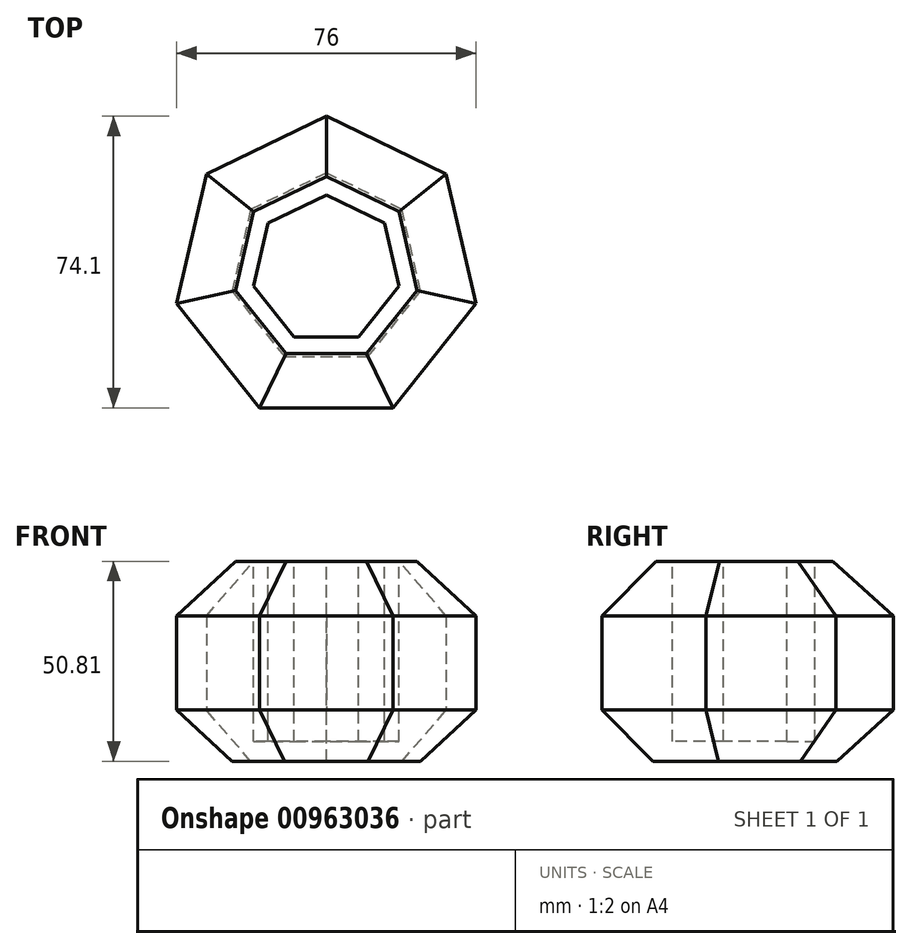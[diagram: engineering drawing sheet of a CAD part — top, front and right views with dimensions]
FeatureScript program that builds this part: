
annotation { "Feature Type Name" : "Feature", "Feature Type Description" : "" }
export const myFeature = defineFeature(function(context is Context, id is Id, definition is map)
    precondition{}
    {
        {
            var Q0;
            Q0=qCreatedBy(makeId("Top.planeOp"),FACE);
            var sketch = newSketch(context, id + "F0", { "sketchPlane" : qUnion([Q0])});
            skCircle(sketch, "E0.cCircle", {"center": v(0, 0) * mm, "radius": 35.12 * mm, "construction": true});
            skLineSegment(sketch, "E0.0", {"start": v(16.91, -35.12) * mm, "end": v(-16.91, -35.12) * mm});
            skLineSegment(sketch, "E0.1", {"start": v(-16.91, -35.12) * mm, "end": v(-38, -8.67) * mm});
            skLineSegment(sketch, "E0.2", {"start": v(-38, -8.67) * mm, "end": v(-30.47, 24.3) * mm});
            skLineSegment(sketch, "E0.3", {"start": v(-30.47, 24.3) * mm, "end": v(0, 38.98) * mm});
            skLineSegment(sketch, "E0.4", {"start": v(0, 38.98) * mm, "end": v(30.47, 24.3) * mm});
            skLineSegment(sketch, "E0.5", {"start": v(30.47, 24.3) * mm, "end": v(38, -8.67) * mm});
            skLineSegment(sketch, "E0.6", {"start": v(38, -8.67) * mm, "end": v(16.91, -35.12) * mm});
            skPoint(sketch, "E0.0.midPoint", {"position": v(0, -35.12) * mm});
            skSolve(sketch);
        }
        {
            var Q0;
            Q0 = qSketchRegion(id + "F0", true);
            extrude(context, id + "F1", {"entities" : qUnion([Q0]), "depth" : 60 * mm, "offsetDistance" : 25 * mm});
        }
        {
            var Q0;
            Q0=makeQuery(id+"F1.opExtrude","CAP_FACE",FACE,{"disambiguationData":[OSD([sQuery(id+"F0.wireOp",EDGE,"E0.0"),sQuery(id+"F0.wireOp",EDGE,"E0.1"),sQuery(id+"F0.wireOp",EDGE,"E0.2"),sQuery(id+"F0.wireOp",EDGE,"E0.3"),sQuery(id+"F0.wireOp",EDGE,"E0.4"),sQuery(id+"F0.wireOp",EDGE,"E0.5"),sQuery(id+"F0.wireOp",EDGE,"E0.6")])],"isStart":true});
            var Q1;
            Q1=makeQuery(id+"F1.opExtrude","CAP_FACE",FACE,{"disambiguationData":[OSD([sQuery(id+"F0.wireOp",EDGE,"E0.0"),sQuery(id+"F0.wireOp",EDGE,"E0.1"),sQuery(id+"F0.wireOp",EDGE,"E0.2"),sQuery(id+"F0.wireOp",EDGE,"E0.3"),sQuery(id+"F0.wireOp",EDGE,"E0.4"),sQuery(id+"F0.wireOp",EDGE,"E0.5"),sQuery(id+"F0.wireOp",EDGE,"E0.6")])],"isStart":false});
            chamfer(context, id + "F2", {"entities" : qUnion([Q0, Q1]), "width" : 18 * mm, "tangentPropagation" : true});
        }
        {
            var Q0;
            Q0=makeQuery(id+"F1.opExtrude","CAP_FACE",FACE,{"disambiguationData":[OSD([sQuery(id+"F0.wireOp",EDGE,"E0.0"),sQuery(id+"F0.wireOp",EDGE,"E0.1"),sQuery(id+"F0.wireOp",EDGE,"E0.2"),sQuery(id+"F0.wireOp",EDGE,"E0.3"),sQuery(id+"F0.wireOp",EDGE,"E0.4"),sQuery(id+"F0.wireOp",EDGE,"E0.5"),sQuery(id+"F0.wireOp",EDGE,"E0.6")])],"isStart":false});
            var sketch = newSketch(context, id + "F3", { "sketchPlane" : qUnion([Q0])});
            skSolve(sketch);
        }
        {
            var Q0;
            {var subQ0=sQuery(id+"F0.wireOp",EDGE,"E0.6");var subQ1=sQuery(id+"F0.wireOp",EDGE,"E0.5");var subQ2=sQuery(id+"F0.wireOp",EDGE,"E0.4");var subQ3=sQuery(id+"F0.wireOp",EDGE,"E0.3");var subQ4=sQuery(id+"F0.wireOp",EDGE,"E0.2");var subQ5=sQuery(id+"F0.wireOp",EDGE,"E0.1");var subQ6=sQuery(id+"F0.wireOp",EDGE,"E0.0");var subQ7=makeQuery(id+"F1.opExtrude","CAP_FACE",FACE,{"disambiguationData":[OSD([subQ6,subQ5,subQ4,subQ3,subQ2,subQ1,subQ0])],"isStart":false});Q0=makeQuery(id+"F3.imprint","IMPRINT",FACE,{"disambiguationData":[TD([[makeQuery(id+"F3.imprint","IMPRINT",EDGE,{"derivedFrom":makeQuery(id+"F2.opChamfer","BLEND_EDGE",EDGE,{"blendedFrom":[makeQuery(id+"F1.opExtrude","CAP_EDGE",EDGE,{"disambiguationData":[OSD([subQ6])],"isStart":false}),subQ7],"blendedInto":[subQ7]})}),1.0]])]});}
            extrude(context, id + "F4", {"entities" : qUnion([Q0]), "operationType" : NewBodyOperationType.REMOVE, "oppositeDirection" : true, "depth" : 50 * mm, "offsetDistance" : 25 * mm});
        }
        {
            var Q0;
            Q0=qCreatedBy(makeId("Front.planeOp"),FACE);
            cPlane(context, id + "F5", {"entities" : qUnion([Q0]), "cplaneType" : CPlaneType.OFFSET, "offset" : 45 * mm, "width" : 150 * mm, "height" : 150 * mm});
        }
        {
            var Q0;
            Q0=qCreatedBy(id+"F5.planeOp",FACE);
            var sketch = newSketch(context, id + "F6", { "sketchPlane" : qUnion([Q0])});
            skLineSegment(sketch, "E1.bottom", {"start": v(-28.5, 55.81) * mm, "end": v(30.37, 55.81) * mm});
            skLineSegment(sketch, "E1.top", {"start": v(-28.5, 65.1) * mm, "end": v(30.37, 65.1) * mm});
            skLineSegment(sketch, "E1.left", {"start": v(-28.5, 55.81) * mm, "end": v(-28.5, 65.1) * mm});
            skLineSegment(sketch, "E1.right", {"start": v(30.37, 55.81) * mm, "end": v(30.37, 65.1) * mm});
            skSolve(sketch);
        }
        {
            var Q0;
            Q0 = qSketchRegion(id + "F6", true);
            extrude(context, id + "F7", {"entities" : qUnion([Q0]), "operationType" : NewBodyOperationType.REMOVE, "oppositeDirection" : true, "depth" : 90 * mm, "offsetDistance" : 25 * mm});
        }
        {
            var Q0;
            Q0=qCreatedBy(id+"F5.planeOp",FACE);
            var sketch = newSketch(context, id + "F8", { "sketchPlane" : qUnion([Q0])});
            skLineSegment(sketch, "E2.bottom", {"start": v(-23.93, 5) * mm, "end": v(31.07, 5) * mm});
            skLineSegment(sketch, "E2.top", {"start": v(-23.93, 0) * mm, "end": v(31.07, 0) * mm});
            skLineSegment(sketch, "E2.left", {"start": v(-23.93, 5) * mm, "end": v(-23.93, 0) * mm});
            skLineSegment(sketch, "E2.right", {"start": v(31.07, 5) * mm, "end": v(31.07, 0) * mm});
            skSolve(sketch);
        }
        {
            var Q0;
            Q0 = qSketchRegion(id + "F8", true);
            extrude(context, id + "F9", {"entities" : qUnion([Q0]), "operationType" : NewBodyOperationType.REMOVE, "oppositeDirection" : true, "depth" : 100 * mm, "offsetDistance" : 25 * mm});
        }
    });
